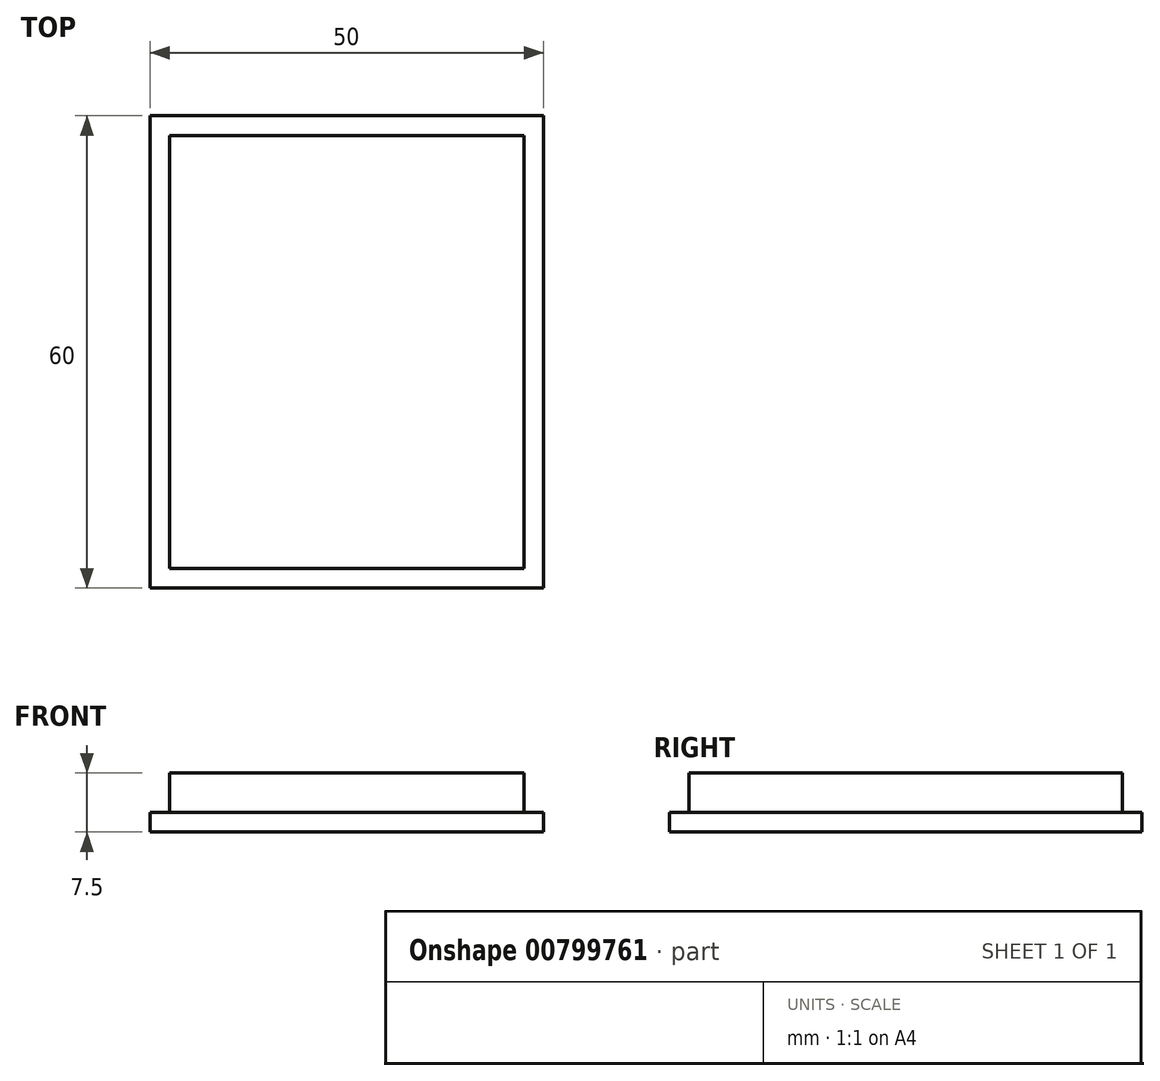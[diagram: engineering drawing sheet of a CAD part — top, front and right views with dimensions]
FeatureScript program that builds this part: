
annotation { "Feature Type Name" : "Feature", "Feature Type Description" : "" }
export const myFeature = defineFeature(function(context is Context, id is Id, definition is map)
    precondition{}
    {
        {
            var Q0;
            Q0=qCreatedBy(makeId("Top.planeOp"),FACE);
            var sketch = newSketch(context, id + "F0", { "sketchPlane" : qUnion([Q0])});
            skLineSegment(sketch, "E0.bottom", {"start": v(-49.82, 60.18) * mm, "end": v(0.18, 60.18) * mm});
            skLineSegment(sketch, "E0.top", {"start": v(-49.82, 0.18) * mm, "end": v(0.18, 0.18) * mm});
            skLineSegment(sketch, "E0.left", {"start": v(-49.82, 60.18) * mm, "end": v(-49.82, 0.18) * mm});
            skLineSegment(sketch, "E0.right", {"start": v(0.18, 60.18) * mm, "end": v(0.18, 0.18) * mm});
            skLineSegment(sketch, "E1.top", {"start": v(-49.82, 2.68) * mm, "end": v(0.18, 2.68) * mm});
            skLineSegment(sketch, "E1.left", {"start": v(-49.82, 0.18) * mm, "end": v(-49.82, 2.68) * mm});
            skLineSegment(sketch, "E1.right", {"start": v(0.18, 0.18) * mm, "end": v(0.18, 2.68) * mm});
            skLineSegment(sketch, "E2.top", {"start": v(-49.82, 57.68) * mm, "end": v(0.18, 57.68) * mm});
            skLineSegment(sketch, "E2.left", {"start": v(-49.82, 60.18) * mm, "end": v(-49.82, 57.68) * mm});
            skLineSegment(sketch, "E2.right", {"start": v(0.18, 60.18) * mm, "end": v(0.18, 57.68) * mm});
            skLineSegment(sketch, "E3.bottom", {"start": v(-49.82, 57.68) * mm, "end": v(-47.32, 57.68) * mm});
            skLineSegment(sketch, "E3.top", {"start": v(-49.82, 2.68) * mm, "end": v(-47.32, 2.68) * mm});
            skLineSegment(sketch, "E3.left", {"start": v(-49.82, 57.68) * mm, "end": v(-49.82, 2.68) * mm});
            skLineSegment(sketch, "E3.right", {"start": v(-47.32, 57.68) * mm, "end": v(-47.32, 2.68) * mm});
            skLineSegment(sketch, "E4.bottom", {"start": v(0.18, 57.68) * mm, "end": v(-2.32, 57.68) * mm});
            skLineSegment(sketch, "E4.top", {"start": v(0.18, 2.68) * mm, "end": v(-2.32, 2.68) * mm});
            skLineSegment(sketch, "E4.left", {"start": v(0.18, 57.68) * mm, "end": v(0.18, 2.68) * mm});
            skLineSegment(sketch, "E4.right", {"start": v(-2.32, 57.68) * mm, "end": v(-2.32, 2.68) * mm});
            skSolve(sketch);
        }
        {
            var Q0;
            {var subQ0=sQuery(id+"F0.wireOp",EDGE,"E3.right");Q0=makeQuery(id+"F0.imprint","IMPRINT",FACE,{"disambiguationData":[TD([[makeQuery(id+"F0.imprint","IMPRINT",EDGE,{"derivedFrom":subQ0}),1.0]])]});}
            extrude(context, id + "F1", {"entities" : qUnion([Q0]), "depth" : 7.5 * mm, "offsetDistance" : 25 * mm});
        }
        {
            var Q0;
            {var subQ4=sQuery(id+"F0.wireOp",EDGE,"E0.top");Q0=makeQuery(id+"F0.imprint","IMPRINT",FACE,{"disambiguationData":[TD([[makeQuery(id+"F0.imprint","IMPRINT",EDGE,{"derivedFrom":subQ4}),1.0]])]});}
            var Q1;
            {var subQ5=sQuery(id+"F0.wireOp",EDGE,"E3.right");Q1=makeQuery(id+"F0.imprint","IMPRINT",FACE,{"disambiguationData":[TD([[makeQuery(id+"F0.imprint","IMPRINT",EDGE,{"derivedFrom":subQ5}),-1.0]])]});}
            var Q2;
            {var subQ3=sQuery(id+"F0.wireOp",EDGE,"E0.bottom");Q2=makeQuery(id+"F0.imprint","IMPRINT",FACE,{"disambiguationData":[TD([[makeQuery(id+"F0.imprint","IMPRINT",EDGE,{"derivedFrom":subQ3}),-1.0]])]});}
            var Q3;
            {var subQ5=sQuery(id+"F0.wireOp",EDGE,"E4.right");Q3=makeQuery(id+"F0.imprint","IMPRINT",FACE,{"disambiguationData":[TD([[makeQuery(id+"F0.imprint","IMPRINT",EDGE,{"derivedFrom":subQ5}),1.0]])]});}
            extrude(context, id + "F2", {"entities" : qUnion([Q0, Q1, Q2, Q3]), "operationType" : NewBodyOperationType.ADD, "depth" : 2.5 * mm, "offsetDistance" : 25 * mm});
        }
    });
